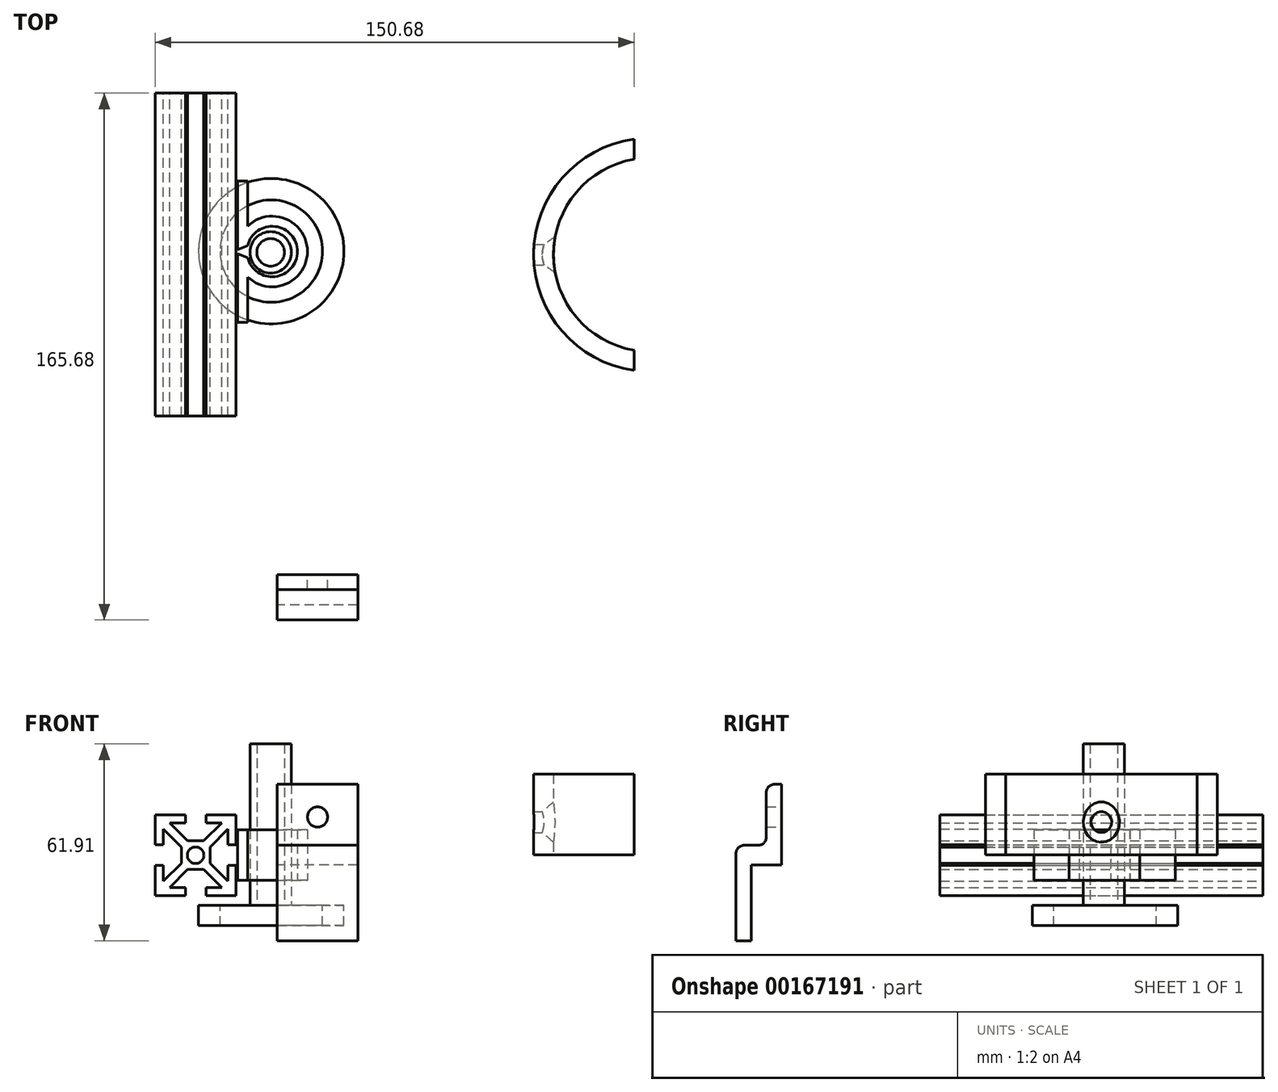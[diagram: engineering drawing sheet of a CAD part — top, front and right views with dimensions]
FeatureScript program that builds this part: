
annotation { "Feature Type Name" : "Feature", "Feature Type Description" : "" }
export const myFeature = defineFeature(function(context is Context, id is Id, definition is map)
    precondition{}
    {
        {
            var Q0;
            Q0=qCreatedBy(makeId("Front.planeOp"),FACE);
            var sketch = newSketch(context, id + "F0", { "sketchPlane" : qUnion([Q0])});
            skCircle(sketch, "E0", {"center": v(-25.66, 3.07) * mm, "radius": 2.6 * mm});
            skLineSegment(sketch, "E1.bottom", {"start": v(-30.17, 7.58) * mm, "end": v(-21.15, 7.58) * mm, "construction": true});
            skLineSegment(sketch, "E1.top", {"start": v(-30.17, -1.44) * mm, "end": v(-21.15, -1.44) * mm, "construction": true});
            skLineSegment(sketch, "E1.left", {"start": v(-30.17, 7.58) * mm, "end": v(-30.17, -1.44) * mm, "construction": true});
            skLineSegment(sketch, "E1.right", {"start": v(-21.15, 7.58) * mm, "end": v(-21.15, -1.44) * mm, "construction": true});
            skPoint(sketch, "E2", {"position": v(-30.17, 3.07) * mm});
            skPoint(sketch, "E3", {"position": v(-25.66, 7.58) * mm});
            skLineSegment(sketch, "E4", {"start": v(-28.2, 7.58) * mm, "end": v(-23.12, 7.58) * mm});
            skLineSegment(sketch, "E5", {"start": v(-23.12, 7.58) * mm, "end": v(-17.47, 13.23) * mm});
            skLineSegment(sketch, "E6", {"start": v(-17.47, 13.23) * mm, "end": v(-22.42, 13.23) * mm});
            skLineSegment(sketch, "E7", {"start": v(-22.42, 13.23) * mm, "end": v(-22.42, 15.77) * mm});
            skLineSegment(sketch, "E8", {"start": v(-22.42, 15.77) * mm, "end": v(-12.96, 15.77) * mm});
            skLineSegment(sketch, "E9", {"start": v(-12.96, 15.77) * mm, "end": v(-12.96, 6.3) * mm});
            skLineSegment(sketch, "E10", {"start": v(-12.96, 6.3) * mm, "end": v(-15.5, 6.3) * mm});
            skLineSegment(sketch, "E11", {"start": v(-15.5, 6.3) * mm, "end": v(-15.5, 11.26) * mm});
            skLineSegment(sketch, "E12", {"start": v(-15.5, 11.26) * mm, "end": v(-21.15, 5.61) * mm});
            skLineSegment(sketch, "E13", {"start": v(-21.15, 5.61) * mm, "end": v(-21.15, 0.53) * mm});
            skLineSegment(sketch, "E14", {"start": v(-21.15, 0.53) * mm, "end": v(-15.5, -5.12) * mm});
            skLineSegment(sketch, "E15", {"start": v(-15.5, -5.12) * mm, "end": v(-15.5, -0.17) * mm});
            skLineSegment(sketch, "E16", {"start": v(-15.5, -0.17) * mm, "end": v(-12.96, -0.17) * mm});
            skLineSegment(sketch, "E17", {"start": v(-12.96, -0.17) * mm, "end": v(-12.96, -9.63) * mm});
            skLineSegment(sketch, "E18", {"start": v(-12.96, -9.63) * mm, "end": v(-22.42, -9.63) * mm});
            skLineSegment(sketch, "E19", {"start": v(-22.42, -9.63) * mm, "end": v(-22.42, -7.09) * mm});
            skLineSegment(sketch, "E20", {"start": v(-22.42, -7.09) * mm, "end": v(-17.47, -7.09) * mm});
            skLineSegment(sketch, "E21", {"start": v(-17.47, -7.09) * mm, "end": v(-23.12, -1.44) * mm});
            skLineSegment(sketch, "E22", {"start": v(-23.12, -1.44) * mm, "end": v(-28.2, -1.44) * mm});
            skLineSegment(sketch, "E23", {"start": v(-28.2, -1.44) * mm, "end": v(-33.85, -7.09) * mm});
            skLineSegment(sketch, "E24", {"start": v(-33.85, -7.09) * mm, "end": v(-28.9, -7.09) * mm});
            skLineSegment(sketch, "E25", {"start": v(-28.9, -7.09) * mm, "end": v(-28.9, -9.63) * mm});
            skLineSegment(sketch, "E26", {"start": v(-28.9, -9.63) * mm, "end": v(-38.36, -9.63) * mm});
            skLineSegment(sketch, "E27", {"start": v(-38.36, -9.63) * mm, "end": v(-38.36, -0.17) * mm});
            skLineSegment(sketch, "E28", {"start": v(-38.36, -0.17) * mm, "end": v(-35.82, -0.17) * mm});
            skLineSegment(sketch, "E29", {"start": v(-35.82, -0.17) * mm, "end": v(-35.82, -5.12) * mm});
            skLineSegment(sketch, "E30", {"start": v(-35.82, -5.12) * mm, "end": v(-30.17, 0.53) * mm});
            skLineSegment(sketch, "E31", {"start": v(-30.17, 0.53) * mm, "end": v(-30.17, 5.61) * mm});
            skLineSegment(sketch, "E32", {"start": v(-30.17, 5.61) * mm, "end": v(-35.82, 11.26) * mm});
            skLineSegment(sketch, "E33", {"start": v(-35.82, 11.26) * mm, "end": v(-35.82, 6.3) * mm});
            skLineSegment(sketch, "E34", {"start": v(-35.82, 6.3) * mm, "end": v(-38.36, 6.3) * mm});
            skLineSegment(sketch, "E35", {"start": v(-38.36, 6.3) * mm, "end": v(-38.36, 15.77) * mm});
            skLineSegment(sketch, "E36", {"start": v(-38.36, 15.77) * mm, "end": v(-28.9, 15.77) * mm});
            skLineSegment(sketch, "E37", {"start": v(-28.9, 15.77) * mm, "end": v(-28.9, 13.23) * mm});
            skLineSegment(sketch, "E38", {"start": v(-28.9, 13.23) * mm, "end": v(-33.85, 13.23) * mm});
            skLineSegment(sketch, "E39", {"start": v(-33.85, 13.23) * mm, "end": v(-28.2, 7.58) * mm});
            skLineSegment(sketch, "E40", {"start": v(-28.9, 15.77) * mm, "end": v(-22.42, 15.77) * mm, "construction": true});
            skLineSegment(sketch, "E41", {"start": v(-12.96, 6.3) * mm, "end": v(-12.96, -0.17) * mm, "construction": true});
            skLineSegment(sketch, "E42", {"start": v(-22.42, -9.63) * mm, "end": v(-28.9, -9.63) * mm, "construction": true});
            skLineSegment(sketch, "E43", {"start": v(-38.36, -0.17) * mm, "end": v(-38.36, 6.3) * mm, "construction": true});
            skPoint(sketch, "E44", {"position": v(-38.36, 3.07) * mm});
            skPoint(sketch, "E45", {"position": v(-25.66, 15.77) * mm});
            skPoint(sketch, "E46", {"position": v(-12.96, 3.07) * mm});
            skPoint(sketch, "E47", {"position": v(-25.66, -9.63) * mm});
            skSolve(sketch);
        }
        {
            var Q0;
            Q0 = qSketchRegion(id + "F0", true);
            extrude(context, id + "F1", {"entities" : qUnion([Q0]), "depth" : 50.8 * mm, "hasSecondDirection" : true, "secondDirectionOppositeDirection" : true, "secondDirectionDepth" : 50.8 * mm});
        }
        {
            var Q0;
            Q0=qCreatedBy(makeId("Top.planeOp"),FACE);
            cPlane(context, id + "F2", {"entities" : qUnion([Q0]), "cplaneType" : CPlaneType.OFFSET, "offset" : 12.7 * mm, "oppositeDirection" : true, "width" : 152.4 * mm, "height" : 152.4 * mm});
        }
        {
            var Q0;
            Q0=qCreatedBy(makeId("Top.planeOp"),FACE);
            cPlane(context, id + "F3", {"entities" : qUnion([Q0]), "cplaneType" : CPlaneType.OFFSET, "offset" : 3.17 * mm, "width" : 152.4 * mm, "height" : 152.4 * mm});
        }
        {
            var Q0;
            Q0=qCreatedBy(id+"F3.planeOp",FACE);
            var sketch = newSketch(context, id + "F4", { "sketchPlane" : qUnion([Q0])});
            skLineSegment(sketch, "E48", {"start": v(-12.47, 23.23) * mm, "end": v(-12.47, 1.64) * mm});
            skLineSegment(sketch, "E49", {"start": v(-12.47, 1.64) * mm, "end": v(-9.3, 2.9) * mm});
            skLineSegment(sketch, "E50", {"start": v(-12.47, 0.37) * mm, "end": v(-12.47, -21.22) * mm});
            skLineSegment(sketch, "E51", {"start": v(-12.47, -21.22) * mm, "end": v(-9.3, -21.22) * mm});
            skLineSegment(sketch, "E52", {"start": v(-9.3, -21.22) * mm, "end": v(-9.3, -7) * mm});
            skLineSegment(sketch, "E53", {"start": v(-12.47, 23.23) * mm, "end": v(-9.3, 23.23) * mm});
            skLineSegment(sketch, "E54", {"start": v(-9.3, 23.23) * mm, "end": v(-9.3, 9.01) * mm});
            skLineSegment(sketch, "E55", {"start": v(-12.47, 0.37) * mm, "end": v(-9.3, -0.9) * mm});
            skArc(sketch, "E56", {"start": v(-9.3, -0.9) * mm, "mid": v(6.35, 1) * mm, "end": v(-9.3, 2.9) * mm});
            skArc(sketch, "E57", {"start": v(-9.3, -7) * mm, "mid": v(9.53, 1) * mm, "end": v(-9.3, 9.01) * mm});
            skLineSegment(sketch, "E58", {"start": v(6.35, 1) * mm, "end": v(9.53, 1) * mm, "construction": true});
            skSolve(sketch);
        }
        {
            var Q0;
            Q0 = qSketchRegion(id + "F4", true);
            extrude(context, id + "F5", {"entities" : qUnion([Q0]), "depth" : 7.94 * mm, "hasSecondDirection" : true, "secondDirectionOppositeDirection" : true, "secondDirectionDepth" : 7.94 * mm});
        }
        {
            var Q0;
            Q0=qCreatedBy(id+"F2.planeOp",FACE);
            var sketch = newSketch(context, id + "F6", { "sketchPlane" : qUnion([Q0])});
            skCircle(sketch, "E59", {"center": v(-1.85, 1.11) * mm, "radius": 16.1 * mm});
            skCircle(sketch, "E60", {"center": v(-1.85, 1.11) * mm, "radius": 22.87 * mm});
            skSolve(sketch);
        }
        {
            var Q0;
            Q0 = qSketchRegion(id + "F6", true);
            extrude(context, id + "F7", {"entities" : qUnion([Q0]), "oppositeDirection" : true, "depth" : 6.35 * mm});
        }
        {
            var Q0;
            Q0=qCreatedBy(id+"F2.planeOp",FACE);
            var sketch = newSketch(context, id + "F8", { "sketchPlane" : qUnion([Q0])});
            skCircle(sketch, "E61", {"center": v(-2.04, 0.74) * mm, "radius": 4.34 * mm});
            skCircle(sketch, "E62", {"center": v(-2.04, 0.74) * mm, "radius": 6.5 * mm});
            skSolve(sketch);
        }
        {
            var Q0;
            Q0 = qSketchRegion(id + "F8", true);
            extrude(context, id + "F9", {"entities" : qUnion([Q0]), "depth" : 50.8 * mm});
        }
        {
            var Q0;
            Q0=qCreatedBy(makeId("Right.planeOp"),FACE);
            var sketch = newSketch(context, id + "F10", { "sketchPlane" : qUnion([Q0])});
            skLineSegment(sketch, "E63", {"start": v(-114.88, -23.81) * mm, "end": v(-110.12, -23.81) * mm});
            skLineSegment(sketch, "E64", {"start": v(-110.12, -23.81) * mm, "end": v(-110.12, 0) * mm});
            skLineSegment(sketch, "E65", {"start": v(-110.12, 0) * mm, "end": v(-103.14, 0) * mm});
            skLineSegment(sketch, "E66", {"start": v(-100.6, 2.54) * mm, "end": v(-100.6, 25.4) * mm});
            skLineSegment(sketch, "E67", {"start": v(-100.6, 25.4) * mm, "end": v(-102.82, 25.4) * mm});
            skLineSegment(sketch, "E68", {"start": v(-105.36, 22.86) * mm, "end": v(-105.36, 8.75) * mm});
            skLineSegment(sketch, "E69", {"start": v(-107.9, 6.21) * mm, "end": v(-112.34, 6.21) * mm});
            skLineSegment(sketch, "E70", {"start": v(-114.88, 3.67) * mm, "end": v(-114.88, -23.81) * mm});
            skPoint(sketch, "E71.visualSharp", {"position": v(-100.6, 0) * mm});
            skPoint(sketch, "E72.visualSharp", {"position": v(-105.36, 25.4) * mm});
            skArc(sketch, "E72.filletArc", {"start": v(-102.82, 25.4) * mm, "mid": v(-104.61, 24.66) * mm, "end": v(-105.36, 22.86) * mm});
            skPoint(sketch, "E73.visualSharp", {"position": v(-105.36, 6.21) * mm});
            skArc(sketch, "E73.filletArc", {"start": v(-107.9, 6.21) * mm, "mid": v(-106.1, 6.96) * mm, "end": v(-105.36, 8.75) * mm});
            skPoint(sketch, "E74.visualSharp", {"position": v(-114.88, 6.21) * mm});
            skArc(sketch, "E74.filletArc", {"start": v(-112.34, 6.21) * mm, "mid": v(-114.14, 5.47) * mm, "end": v(-114.88, 3.67) * mm});
            skLineSegment(sketch, "E75", {"start": v(-100.6, 2.54) * mm, "end": v(-100.6, 0) * mm});
            skLineSegment(sketch, "E76", {"start": v(-103.14, 0) * mm, "end": v(-100.6, 0) * mm});
            skSolve(sketch);
        }
        {
            var Q0;
            Q0 = qSketchRegion(id + "F10", true);
            extrude(context, id + "F11", {"entities" : qUnion([Q0]), "depth" : 25.4 * mm});
        }
        {
            var Q0;
            Q0=qCreatedBy(id+"F3.planeOp",FACE);
            var sketch = newSketch(context, id + "F12", { "sketchPlane" : qUnion([Q0])});
            skArc(sketch, "E77", {"start": v(112.32, 30.05) * mm, "mid": v(86.92, 0) * mm, "end": v(112.32, -30.05) * mm});
            skArc(sketch, "E78", {"start": v(112.32, 36.4) * mm, "mid": v(80.64, 0) * mm, "end": v(112.32, -36.4) * mm});
            skLineSegment(sketch, "E79", {"start": v(112.32, 36.4) * mm, "end": v(112.32, 30.05) * mm});
            skLineSegment(sketch, "E80", {"start": v(112.32, -30.05) * mm, "end": v(112.32, -36.4) * mm});
            skPoint(sketch, "E81.positionSnap0", {"position": v(86.92, 0) * mm});
            skLineSegment(sketch, "E82", {"start": v(112.32, 30.05) * mm, "end": v(112.32, -30.05) * mm, "construction": true});
            skSolve(sketch);
        }
        {
            var Q0;
            Q0 = qSketchRegion(id + "F12", true);
            extrude(context, id + "F13", {"entities" : qUnion([Q0]), "depth" : 25.4 * mm});
        }
        {
            var Q0;
            Q0=makeQuery(id+"F11.opExtrude","SWEPT_FACE",FACE,{"disambiguationData":[OSD([sQuery(id+"F10.wireOp",EDGE,"E66"),sQuery(id+"F10.wireOp",EDGE,"E75")])]});
            var sketch = newSketch(context, id + "F14", { "sketchPlane" : qUnion([Q0])});
            skCircle(sketch, "E83", {"center": v(-12.7, 15.08) * mm, "radius": 3.18 * mm});
            skLineSegment(sketch, "E84", {"start": v(-25.4, 15.08) * mm, "end": v(0, 15.08) * mm, "construction": true});
            skSolve(sketch);
        }
        {
            var Q0;
            Q0 = qSketchRegion(id + "F14", true);
            extrude(context, id + "F15", {"entities" : qUnion([Q0]), "operationType" : NewBodyOperationType.REMOVE, "endBound" : BoundingType.THROUGH_ALL, "oppositeDirection" : true, "depth" : 25.4 * mm});
        }
        {
            var Q0;
            Q0=makeQuery(id+"F13.opExtrude","SWEPT_FACE",FACE,{"disambiguationData":[OSD([sQuery(id+"F12.wireOp",EDGE,"E80")])]});
            var sketch = newSketch(context, id + "F16", { "sketchPlane" : qUnion([Q0])});
            skCircle(sketch, "E85", {"center": v(0, 13.5) * mm, "radius": 3.26 * mm});
            skLineSegment(sketch, "E86", {"start": v(-36.4, 3.18) * mm, "end": v(36.4, 3.18) * mm, "construction": true});
            skPoint(sketch, "E87", {"position": v(0, 3.18) * mm});
            skSolve(sketch);
        }
        {
            var Q0;
            Q0 = qSketchRegion(id + "F16", true);
            extrude(context, id + "F17", {"entities" : qUnion([Q0]), "operationType" : NewBodyOperationType.REMOVE, "oppositeDirection" : true, "depth" : 50.8 * mm});
        }
        {
            var Q0;
            Q0=makeQuery(id+"F17.boolean.opBoolean","INTERSECT",EDGE,{"derivedFrom":[makeQuery(id+"F13.opExtrude","SWEPT_FACE",FACE,{"disambiguationData":[OSD([sQuery(id+"F12.wireOp",EDGE,"E77")])]}),makeQuery(id+"F17.opExtrude","SWEPT_FACE",FACE,{"disambiguationData":[OSD([sQuery(id+"F16.wireOp",EDGE,"E85")])]})]});
            chamfer(context, id + "F18", {"entities" : qUnion([Q0]), "chamferType" : ChamferType.OFFSET_ANGLE, "width" : 3.56 * mm, "oppositeDirection" : false, "angle" : 41 * degree});
        }
    });
